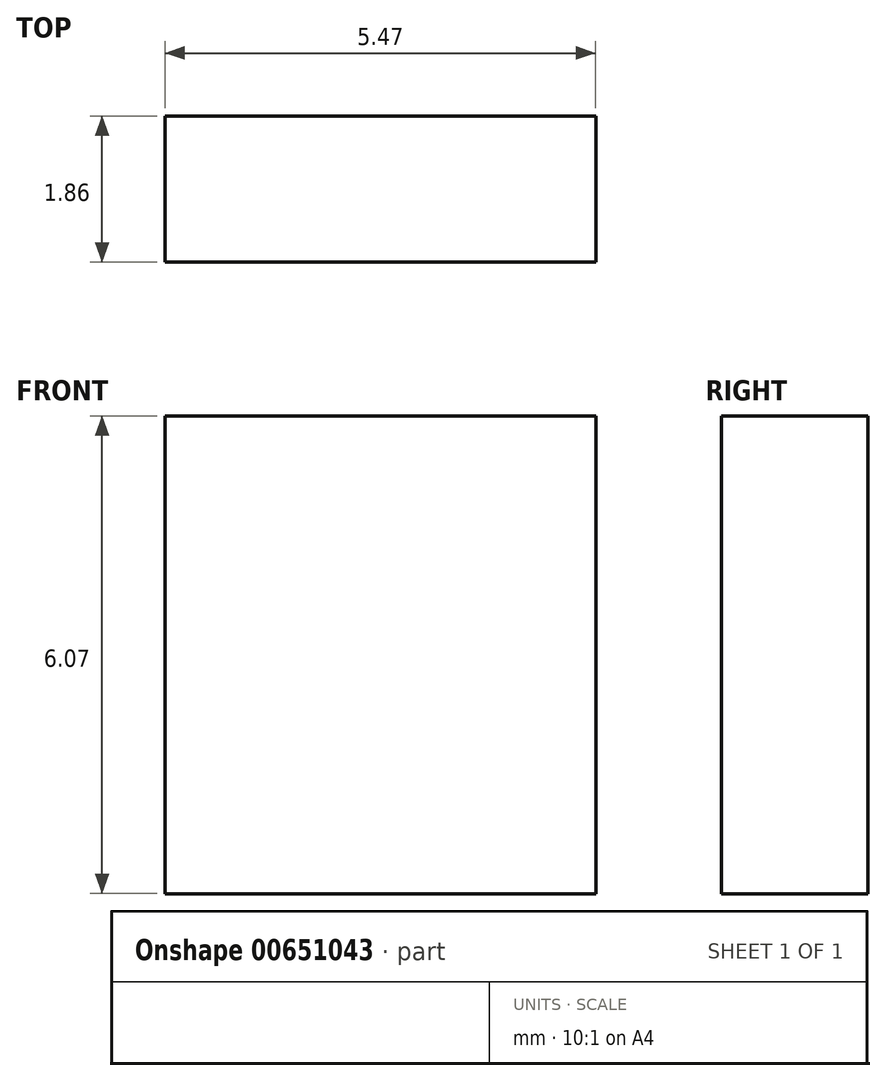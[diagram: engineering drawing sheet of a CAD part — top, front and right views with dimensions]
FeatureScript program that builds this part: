
annotation { "Feature Type Name" : "Feature", "Feature Type Description" : "" }
export const myFeature = defineFeature(function(context is Context, id is Id, definition is map)
    precondition{}
    {
        {
            var Q0;
            Q0=qCreatedBy(makeId("Front.planeOp"),FACE);
            var sketch = newSketch(context, id + "F0", { "sketchPlane" : qUnion([Q0])});
            skLineSegment(sketch, "E0.bottom", {"start": v(-7.35, 4.98) * mm, "end": v(-1.88, 4.98) * mm});
            skLineSegment(sketch, "E0.top", {"start": v(-7.35, -1.1) * mm, "end": v(-1.88, -1.1) * mm});
            skLineSegment(sketch, "E0.left", {"start": v(-7.35, 4.98) * mm, "end": v(-7.35, -1.1) * mm});
            skLineSegment(sketch, "E0.right", {"start": v(-1.88, 4.98) * mm, "end": v(-1.88, -1.1) * mm});
            skSolve(sketch);
        }
        {
            var Q0;
            Q0 = qSketchRegion(id + "F0", true);
            extrude(context, id + "F1", {"entities" : qUnion([Q0]), "depth" : 1.86 * mm, "offsetDistance" : 25 * mm});
        }
    });
